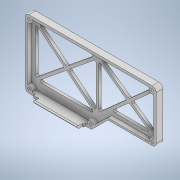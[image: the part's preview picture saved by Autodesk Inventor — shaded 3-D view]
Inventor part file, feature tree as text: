
AUTODESK INVENTOR PART (.ipt)
format: ipt  version: 2021 (Build 250183000, 183)  size: 547,840 bytes
history: native  units: mm
features: sketch x23, extrude x21, fillet x5, hole x2, chamfer x2
ambient origin geometry x8: Origin, YZ Plane, XZ Plane, XY Plane, X Axis, Y Axis, Z Axis, Center Point
bodies: Solid1 (feature_tree)
feature tree (53):
  extrude  "Extrusion1"  Depth=100.0mm
  extrude  "Extrusion2"  Depth=50.0mm
  hole  "Hole1"  [1 undecoded]
  extrude  "Extrusion3"  Depth=50.0mm
  extrude  "Extrusion4"  Depth=3.0mm
  extrude  "Extrusion5"  Depth=3.0mm
  fillet  "Fillet1"  Radius=49.0mm
  extrude  "Extrusion6"  Depth=49.0mm
  extrude  "Extrusion7"  Depth=5.0mm
  extrude  "Extrusion8"  Depth=5.0mm
  chamfer  "Chamfer1"  Distance=3.0mm
  extrude  "Extrusion9"  Depth=12.5mm
  fillet  "Fillet2"  Radius=63.1mm
  extrude  "Extrusion11"  Depth=3.0mm
  extrude  "Extrusion12"  Depth=2.0mm
  chamfer  "Chamfer2"  Distance=3.0mm
  extrude  "Extrusion13"  Depth=3.0mm
  extrude  "Extrusion14"  Depth=5.0mm
  extrude  "Extrusion15"  Depth=3.0mm TaperAngle=0.0deg
  fillet  "Fillet3"  Radius=5.0mm
  fillet  "Fillet4"  Radius=2.0mm
  hole  "Hole2"  [1 undecoded]
  extrude  "Extrusion20"  Depth=5.0mm
  extrude  "Extrusion21"  Depth=1.2mm
  fillet  "Fillet5"  Radius=3.0mm
  extrude  "Extrusion22"  Depth=14.0mm
  extrude  "Extrusion23"  Depth=1.2mm
  extrude  "Extrusion24"  Depth=5.0mm
  extrude  "Extrusion25"  Depth=12.0mm
  extrude  "Extrusion26"  Depth=3.0mm TaperAngle=0.0deg
  sketch  "Sketch1"  dims[d0=52.0mm d1=100.0mm]
  sketch  "Sketch2"  dims[d2=26.0mm d3=50.0mm]
  sketch  "Sketch3"  dims[d4=2.0mm d5=0.0mm d6=3.0mm]
  sketch  "Sketch4"  dims[d7=3.0mm d8=50.0mm]
  sketch  "Sketch5"  dims[d9=3.0mm d10=97.0mm]
  sketch  "Sketch6"  dims[d11=15.0mm d12=3.0mm d13=49.0mm]
  sketch  "Sketch7"  dims[d14=97.0mm d15=49.0mm]
  sketch  "Sketch8"  dims[d16=2.0mm d17=5.0mm]
  sketch  "Sketch9"  dims[d18=2.0mm d19=5.0mm]
  sketch  "Sketch10"  dims[d20=2.0mm]
  sketch  "Sketch12"  dims[d21=5.0mm]
  sketch  "Sketch13"  dims[d22=2.0mm]
  sketch  "Sketch14"  dims[d23=5.0mm]
  sketch  "Sketch15"  dims[d24=2.0mm]
  sketch  "Sketch16"  dims[d25=5.0mm d26=3.0mm d27=0.0mm]
  sketch  "Sketch17"  dims[d28=2.0mm d29=6.0mm d30=5.0mm d31=2.0mm d32=90.0deg d33=10.0mm d34=20.594885mm d35=12.5mm d36=63.1mm]
  sketch  "Sketch23"  dims[d37=3.0mm d38=0.0mm d39=50.673mm]
  sketch  "Sketch24"  dims[d40=3.0mm d41=0.0mm d42=2.0mm]
  sketch  "Sketch25"  dims[d43=2.0mm]
  sketch  "Sketch26"  dims[d44=2.0mm]
  sketch  "Sketch27"  dims[d45=1.5mm d46=3.0mm d47=0.0mm]
  sketch  "Sketch28"  dims[d48=3.0mm d49=7.6mm]
  sketch  "Sketch29"  dims[d50=46.4mm d51=6.7mm d52=3.0mm d53=0.0mm d54=5.0mm d55=2.0mm d56=12.0mm d57=0.0mm d58=1.4mm d59=1.2mm d60=3.0mm d61=14.0mm d62=1.2mm d63=1.4mm d64=12.0mm d65=3.0mm d66=0.0mm d67=1.0mm d68=2.0mm d69=45.0deg d70=1.2mm d71=3.0mm d72=0.0mm d73=1.0mm d77=3.0mm d78=0.0mm d79=3.0mm d80=3.0mm d81=3.0mm d82=3.0mm d83=3.0mm d84=3.0mm d85=3.0mm d86=48.0mm d87=2.0mm d88=0.0mm d89=8.4mm d90=2.0mm d91=45.0deg d92=1.2mm d93=3.0mm d94=0.0mm d95=7.6mm d96=5.0mm d97=0.0mm d98=2.0mm d99=2.0mm d100=2.0mm d101=2.0mm d102=2.0mm d103=2.0mm d104=0.0mm d105=1.0mm d106=1.0mm d107=2.0mm d108=6.0mm d109=5.0mm d110=2.0mm d111=90.0deg d112=4.0mm d113=20.594885mm d146=6.5mm d147=5.0mm d148=2.0mm d149=0.0mm d150=0.3mm d151=0.3mm d152=2.0mm d153=0.0mm d154=3.0mm d155=2.0mm d156=2.0mm d157=2.0mm d158=2.0mm d159=0.0mm d160=1.5mm d161=2.811mm d162=12.0mm d163=33.2mm d164=2.0mm d165=0.0mm d166=2.581mm d167=8.726646mm d168=2.0mm d169=33.2mm d170=0.0mm d171=1.2mm d172=33.2mm d173=0.0mm d174=0.1mm d175=0.1mm d176=5.0mm d177=0.0mm d74=0.872665mm d75=0.872665mm d76=0.5mm d114=0.75mm d115=20.594885mm d116=0.0625mm d117=0.75mm d118=0.375mm]
note: 2 required parameter values undecoded (feature->parameter linkage not recoverable at this tier; creation-order binding heuristic only, values carry confidence <= 0.55)
